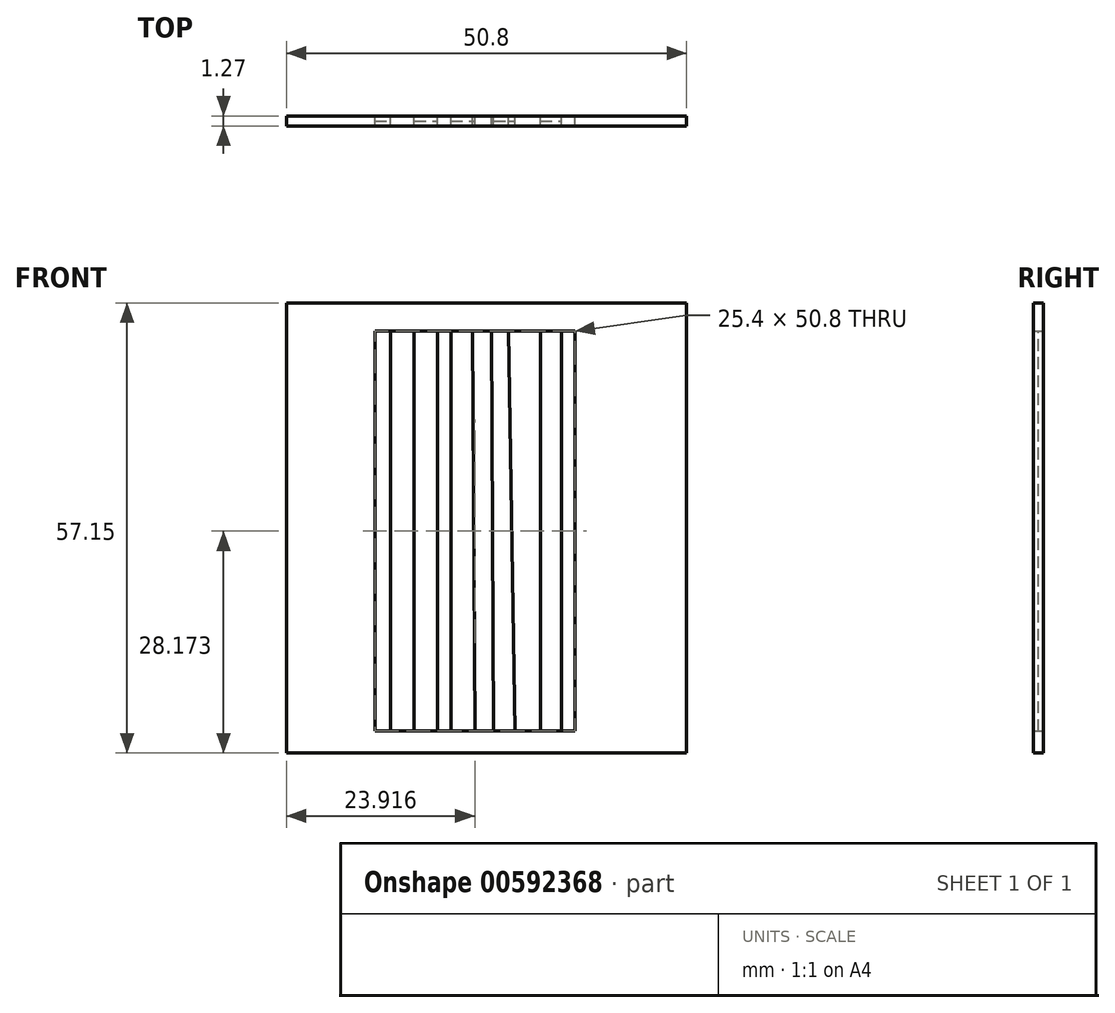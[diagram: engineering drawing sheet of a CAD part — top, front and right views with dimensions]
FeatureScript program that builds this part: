
annotation { "Feature Type Name" : "Feature", "Feature Type Description" : "" }
export const myFeature = defineFeature(function(context is Context, id is Id, definition is map)
    precondition{}
    {
        {
            var Q0;
            Q0=qCreatedBy(makeId("Front.planeOp"),FACE);
            var sketch = newSketch(context, id + "F0", { "sketchPlane" : qUnion([Q0])});
            skLineSegment(sketch, "E0.bottom", {"start": v(-46.54, 12) * mm, "end": v(4.26, 12) * mm});
            skLineSegment(sketch, "E0.top", {"start": v(-46.54, -45.15) * mm, "end": v(4.26, -45.15) * mm});
            skLineSegment(sketch, "E0.left", {"start": v(-46.54, 12) * mm, "end": v(-46.54, -45.15) * mm});
            skLineSegment(sketch, "E0.right", {"start": v(4.26, 12) * mm, "end": v(4.26, -45.15) * mm});
            skLineSegment(sketch, "E1.bottom", {"start": v(-35.32, 8.42) * mm, "end": v(-9.92, 8.42) * mm});
            skLineSegment(sketch, "E1.top", {"start": v(-35.32, -42.38) * mm, "end": v(-9.92, -42.38) * mm});
            skLineSegment(sketch, "E1.left", {"start": v(-35.32, 8.42) * mm, "end": v(-35.32, -42.38) * mm});
            skLineSegment(sketch, "E1.right", {"start": v(-9.92, 8.42) * mm, "end": v(-9.92, -42.38) * mm});
            skLineSegment(sketch, "E2", {"start": v(-22.62, -42.38) * mm, "end": v(-9.92, -42.38) * mm});
            skLineSegment(sketch, "E3", {"start": v(-9.92, 8.42) * mm, "end": v(-35.32, 8.42) * mm});
            skLineSegment(sketch, "E4", {"start": v(-17.52, -42.38) * mm, "end": v(-22.91, -42.38) * mm});
            skLineSegment(sketch, "E5", {"start": v(-9.92, -42.38) * mm, "end": v(-11.31, -42.38) * mm});
            skLineSegment(sketch, "E6", {"start": v(-33.3, 8.42) * mm, "end": v(-33.3, -42.38) * mm});
            skLineSegment(sketch, "E7", {"start": v(-33.3, -42.38) * mm, "end": v(-30.32, -42.38) * mm});
            skLineSegment(sketch, "E8", {"start": v(-30.32, -42.38) * mm, "end": v(-30.32, 8.42) * mm});
            skLineSegment(sketch, "E9", {"start": v(-30.32, 8.42) * mm, "end": v(-27.33, 8.42) * mm});
            skLineSegment(sketch, "E10", {"start": v(-27.33, 8.42) * mm, "end": v(-27.33, -42.38) * mm});
            skLineSegment(sketch, "E11", {"start": v(-27.33, -42.38) * mm, "end": v(-25.67, -42.38) * mm});
            skLineSegment(sketch, "E12", {"start": v(-25.67, -42.38) * mm, "end": v(-25.67, 8.42) * mm});
            skLineSegment(sketch, "E13", {"start": v(-25.67, 8.42) * mm, "end": v(-22.91, 8.42) * mm});
            skLineSegment(sketch, "E14", {"start": v(-22.91, 8.42) * mm, "end": v(-22.62, -42.38) * mm});
            skLineSegment(sketch, "E15", {"start": v(-20.22, -42.38) * mm, "end": v(-20.5, 8.42) * mm});
            skLineSegment(sketch, "E16", {"start": v(-20.5, 8.42) * mm, "end": v(-18.36, 8.42) * mm});
            skLineSegment(sketch, "E17", {"start": v(-18.36, 8.42) * mm, "end": v(-17.52, -42.38) * mm});
            skPoint(sketch, "E18.endSnap0", {"position": v(-16.27, -42.38) * mm});
            skPoint(sketch, "E18.end.orphan", {"position": v(-16.27, 8.42) * mm});
            skLineSegment(sketch, "E19", {"start": v(-14.3, -42.38) * mm, "end": v(-14.3, 8.42) * mm});
            skLineSegment(sketch, "E20", {"start": v(-14.3, 8.42) * mm, "end": v(-11.62, 8.42) * mm});
            skLineSegment(sketch, "E21", {"start": v(-11.62, 8.42) * mm, "end": v(-11.62, -42.38) * mm});
            skSolve(sketch);
        }
        {
            var Q0;
            {var subQ0=sQuery(id+"F0.wireOp",EDGE,"E1.left");Q0=makeQuery(id+"F0.imprint","IMPRINT",FACE,{"disambiguationData":[TD([[makeQuery(id+"F0.imprint","IMPRINT",EDGE,{"derivedFrom":subQ0}),1.0]])]});}
            var Q1;
            {var subQ0=sQuery(id+"F0.wireOp",EDGE,"E8");Q1=makeQuery(id+"F0.imprint","IMPRINT",FACE,{"disambiguationData":[TD([[makeQuery(id+"F0.imprint","IMPRINT",EDGE,{"derivedFrom":subQ0}),-1.0]])]});}
            var Q2;
            {var subQ0=sQuery(id+"F0.wireOp",EDGE,"E12");Q2=makeQuery(id+"F0.imprint","IMPRINT",FACE,{"disambiguationData":[TD([[makeQuery(id+"F0.imprint","IMPRINT",EDGE,{"derivedFrom":subQ0}),-1.0]])]});}
            var Q3;
            {var subQ2=sQuery(id+"F0.wireOp",EDGE,"E15");Q3=makeQuery(id+"F0.imprint","IMPRINT",FACE,{"disambiguationData":[TD([[makeQuery(id+"F0.imprint","IMPRINT",EDGE,{"derivedFrom":subQ2}),-1.0]])]});}
            var Q4;
            {var subQ0=sQuery(id+"F0.wireOp",EDGE,"E19");Q4=makeQuery(id+"F0.imprint","IMPRINT",FACE,{"disambiguationData":[TD([[makeQuery(id+"F0.imprint","IMPRINT",EDGE,{"derivedFrom":subQ0}),-1.0]])]});}
            extrude(context, id + "F1", {"entities" : qUnion([Q0, Q1, Q2, Q3, Q4]), "depth" : 0.64 * mm, "offsetDistance" : 25.4 * mm});
        }
        {
            var Q0;
            {var subQ0=sQuery(id+"F0.wireOp",EDGE,"E6");Q0=makeQuery(id+"F0.imprint","IMPRINT",FACE,{"disambiguationData":[TD([[makeQuery(id+"F0.imprint","IMPRINT",EDGE,{"derivedFrom":subQ0}),1.0]])]});}
            var Q1;
            {var subQ0=sQuery(id+"F0.wireOp",EDGE,"E10");Q1=makeQuery(id+"F0.imprint","IMPRINT",FACE,{"disambiguationData":[TD([[makeQuery(id+"F0.imprint","IMPRINT",EDGE,{"derivedFrom":subQ0}),1.0]])]});}
            var Q2;
            {var subQ0=sQuery(id+"F0.wireOp",EDGE,"E14");Q2=makeQuery(id+"F0.imprint","IMPRINT",FACE,{"disambiguationData":[TD([[makeQuery(id+"F0.imprint","IMPRINT",EDGE,{"derivedFrom":subQ0}),1.0]])]});}
            var Q3;
            {var subQ0=sQuery(id+"F0.wireOp",EDGE,"E17");Q3=makeQuery(id+"F0.imprint","IMPRINT",FACE,{"disambiguationData":[TD([[makeQuery(id+"F0.imprint","IMPRINT",EDGE,{"derivedFrom":subQ0}),1.0]])]});}
            var Q4;
            {var subQ1=sQuery(id+"F0.wireOp",EDGE,"E1.right");Q4=makeQuery(id+"F0.imprint","IMPRINT",FACE,{"disambiguationData":[TD([[makeQuery(id+"F0.imprint","IMPRINT",EDGE,{"derivedFrom":subQ1}),-1.0]])]});}
            extrude(context, id + "F2", {"entities" : qUnion([Q0, Q1, Q2, Q3, Q4]), "depth" : 1.27 * mm, "offsetDistance" : 25.4 * mm});
        }
        {
            var Q0;
            Q0=makeQuery(id+"F0.imprint","IMPRINT",FACE,{"disambiguationData":[TD([[makeQuery(id+"F0.imprint","IMPRINT",EDGE,{"derivedFrom":sQuery(id+"F0.wireOp",EDGE,"E0.bottom")}),-1.0]])]});
            extrude(context, id + "F3", {"entities" : qUnion([Q0]), "depth" : 1.27 * mm, "offsetDistance" : 25.4 * mm});
        }
    });
